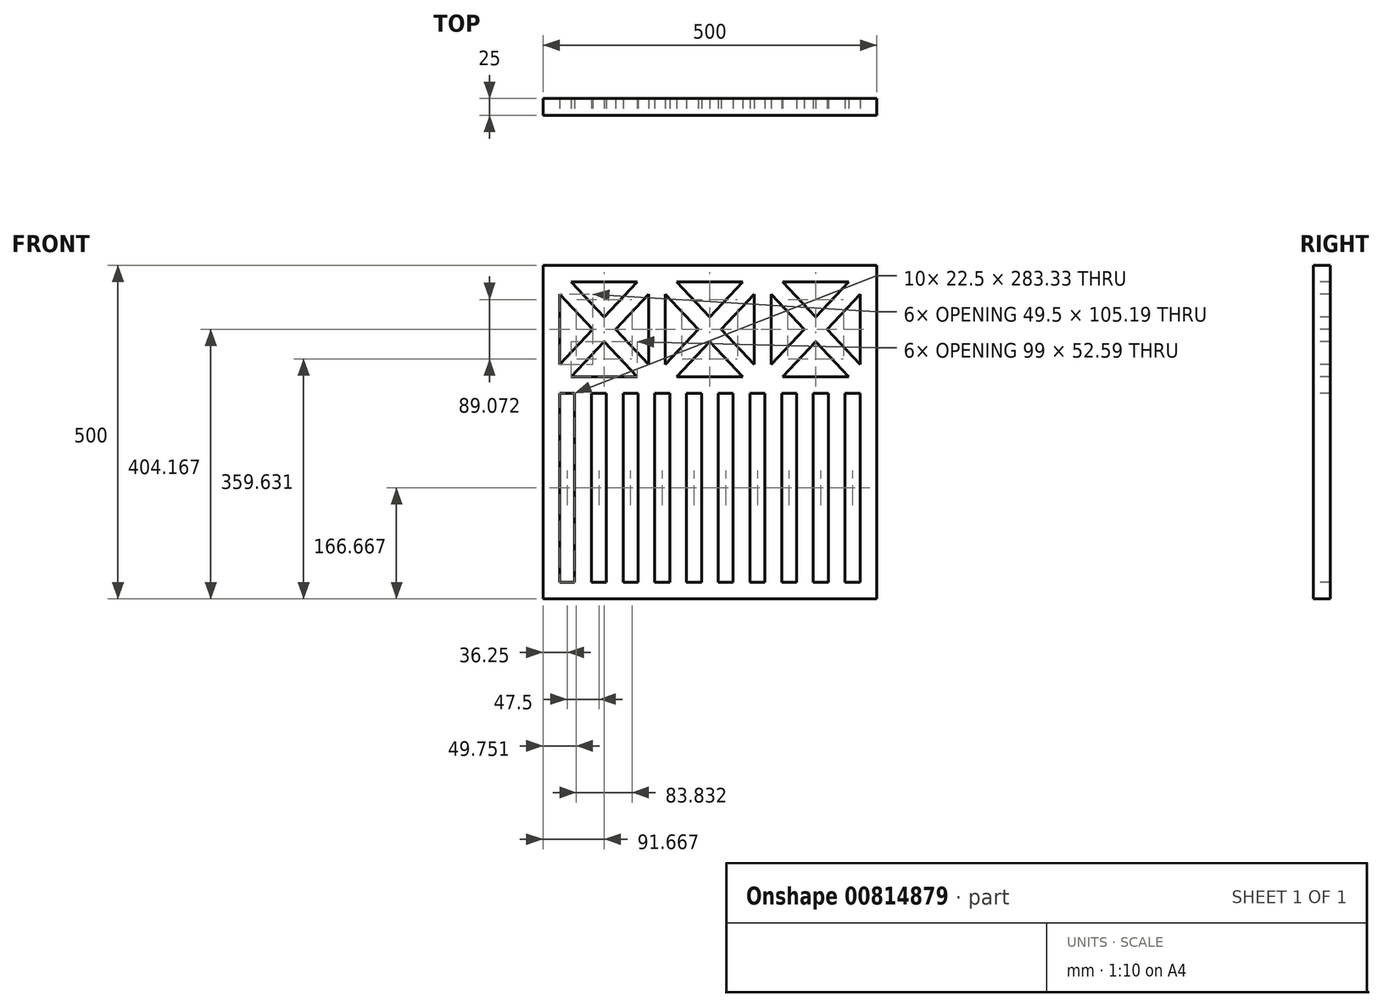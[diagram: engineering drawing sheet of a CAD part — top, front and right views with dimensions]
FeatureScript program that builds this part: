
annotation { "Feature Type Name" : "Feature", "Feature Type Description" : "" }
export const myFeature = defineFeature(function(context is Context, id is Id, definition is map)
    precondition{}
    {
        {
            var Q0;
            Q0=qCreatedBy(makeId("Front.planeOp"),FACE);
            var sketch = newSketch(context, id + "F0", { "sketchPlane" : qUnion([Q0])});
            skLineSegment(sketch, "E0.bottom", {"start": v(0, 0) * mm, "end": v(500, 0) * mm});
            skLineSegment(sketch, "E0.top", {"start": v(0, 500) * mm, "end": v(500, 500) * mm});
            skLineSegment(sketch, "E0.left", {"start": v(0, 0) * mm, "end": v(0, 500) * mm});
            skLineSegment(sketch, "E0.right", {"start": v(500, 0) * mm, "end": v(500, 500) * mm});
            skLineSegment(sketch, "E1.0", {"start": v(25, 25) * mm, "end": v(475, 25) * mm});
            skLineSegment(sketch, "E1.1", {"start": v(25, 25) * mm, "end": v(25, 475) * mm});
            skLineSegment(sketch, "E1.2", {"start": v(25, 475) * mm, "end": v(475, 475) * mm});
            skLineSegment(sketch, "E1.3", {"start": v(475, 25) * mm, "end": v(475, 475) * mm});
            skLineSegment(sketch, "E2", {"start": v(0, 500) * mm, "end": v(25, 475) * mm});
            skLineSegment(sketch, "E3", {"start": v(475, 475) * mm, "end": v(500, 500) * mm});
            skLineSegment(sketch, "E4", {"start": v(500, 0) * mm, "end": v(475, 25) * mm});
            skLineSegment(sketch, "E5", {"start": v(25, 25) * mm, "end": v(0, 0) * mm});
            skLineSegment(sketch, "E6", {"start": v(25, 333.33) * mm, "end": v(475, 333.33) * mm});
            skLineSegment(sketch, "E7", {"start": v(475, 308.33) * mm, "end": v(25, 308.33) * mm});
            skLineSegment(sketch, "E8", {"start": v(158.33, 475) * mm, "end": v(158.33, 333.33) * mm});
            skLineSegment(sketch, "E9", {"start": v(183.33, 475) * mm, "end": v(183.33, 333.33) * mm});
            skLineSegment(sketch, "E10", {"start": v(316.67, 475) * mm, "end": v(316.67, 333.33) * mm});
            skLineSegment(sketch, "E11", {"start": v(341.67, 475) * mm, "end": v(341.67, 333.33) * mm});
            skLineSegment(sketch, "E12", {"start": v(25, 475) * mm, "end": v(158.33, 333.33) * mm, "construction": true});
            skLineSegment(sketch, "E13.0", {"start": v(25, 456.76) * mm, "end": v(141.17, 333.33) * mm});
            skLineSegment(sketch, "E14.0", {"start": v(42.17, 475) * mm, "end": v(158.33, 351.57) * mm});
            skLineSegment(sketch, "E15", {"start": v(158.33, 475) * mm, "end": v(25, 333.33) * mm, "construction": true});
            skLineSegment(sketch, "E16.0", {"start": v(158.33, 456.76) * mm, "end": v(108.83, 404.17) * mm});
            skLineSegment(sketch, "E17.trimOffspring", {"start": v(91.67, 385.93) * mm, "end": v(42.17, 333.33) * mm});
            skLineSegment(sketch, "E18.0", {"start": v(141.17, 475) * mm, "end": v(91.67, 422.4) * mm});
            skLineSegment(sketch, "E19.trimOffspring", {"start": v(74.5, 404.17) * mm, "end": v(25, 351.57) * mm});
            skLineSegment(sketch, "E20.1.0.0", {"start": v(200.5, 475) * mm, "end": v(316.67, 351.57) * mm});
            skLineSegment(sketch, "E20.1.0.1", {"start": v(183.33, 456.76) * mm, "end": v(299.5, 333.33) * mm});
            skLineSegment(sketch, "E20.1.0.2", {"start": v(299.5, 475) * mm, "end": v(250, 422.4) * mm});
            skLineSegment(sketch, "E20.1.0.3", {"start": v(316.67, 456.76) * mm, "end": v(267.17, 404.17) * mm});
            skLineSegment(sketch, "E20.1.0.4", {"start": v(250, 385.93) * mm, "end": v(200.5, 333.33) * mm});
            skLineSegment(sketch, "E20.1.0.5", {"start": v(232.83, 404.17) * mm, "end": v(183.33, 351.57) * mm});
            skLineSegment(sketch, "E20.2.0.0", {"start": v(358.83, 475) * mm, "end": v(475, 351.57) * mm});
            skLineSegment(sketch, "E20.2.0.1", {"start": v(341.67, 456.76) * mm, "end": v(457.83, 333.33) * mm});
            skLineSegment(sketch, "E20.2.0.2", {"start": v(457.83, 475) * mm, "end": v(408.33, 422.4) * mm});
            skLineSegment(sketch, "E20.2.0.3", {"start": v(475, 456.76) * mm, "end": v(425.5, 404.17) * mm});
            skLineSegment(sketch, "E20.2.0.4", {"start": v(408.33, 385.93) * mm, "end": v(358.83, 333.33) * mm});
            skLineSegment(sketch, "E20.2.0.5", {"start": v(391.17, 404.17) * mm, "end": v(341.67, 351.57) * mm});
            skLineSegment(sketch, "E20.direction1", {"start": v(42.17, 475) * mm, "end": v(200.5, 475) * mm, "construction": true});
            skLineSegment(sketch, "E21", {"start": v(47.5, 308.33) * mm, "end": v(47.5, 25) * mm});
            skLineSegment(sketch, "E22", {"start": v(72.5, 308.33) * mm, "end": v(72.5, 25) * mm});
            skLineSegment(sketch, "E23.1.0.0", {"start": v(120, 308.33) * mm, "end": v(120, 25) * mm});
            skLineSegment(sketch, "E23.1.0.1", {"start": v(95, 308.33) * mm, "end": v(95, 25) * mm});
            skLineSegment(sketch, "E23.2.0.0", {"start": v(167.5, 308.33) * mm, "end": v(167.5, 25) * mm});
            skLineSegment(sketch, "E23.2.0.1", {"start": v(142.5, 308.33) * mm, "end": v(142.5, 25) * mm});
            skLineSegment(sketch, "E23.3.0.0", {"start": v(215, 308.33) * mm, "end": v(215, 25) * mm});
            skLineSegment(sketch, "E23.3.0.1", {"start": v(190, 308.33) * mm, "end": v(190, 25) * mm});
            skLineSegment(sketch, "E23.4.0.0", {"start": v(262.5, 308.33) * mm, "end": v(262.5, 25) * mm});
            skLineSegment(sketch, "E23.4.0.1", {"start": v(237.5, 308.33) * mm, "end": v(237.5, 25) * mm});
            skLineSegment(sketch, "E23.5.0.0", {"start": v(310, 308.33) * mm, "end": v(310, 25) * mm});
            skLineSegment(sketch, "E23.5.0.1", {"start": v(285, 308.33) * mm, "end": v(285, 25) * mm});
            skLineSegment(sketch, "E23.6.0.0", {"start": v(357.5, 308.33) * mm, "end": v(357.5, 25) * mm});
            skLineSegment(sketch, "E23.6.0.1", {"start": v(332.5, 308.33) * mm, "end": v(332.5, 25) * mm});
            skLineSegment(sketch, "E23.7.0.0", {"start": v(405, 308.33) * mm, "end": v(405, 25) * mm});
            skLineSegment(sketch, "E23.7.0.1", {"start": v(380, 308.33) * mm, "end": v(380, 25) * mm});
            skLineSegment(sketch, "E23.8.0.0", {"start": v(452.5, 308.33) * mm, "end": v(452.5, 25) * mm});
            skLineSegment(sketch, "E23.8.0.1", {"start": v(427.5, 308.33) * mm, "end": v(427.5, 25) * mm});
            skLineSegment(sketch, "E23.direction1", {"start": v(72.5, 25) * mm, "end": v(120, 25) * mm, "construction": true});
            skSolve(sketch);
        }
        {
            var Q0;
            Q0=makeQuery(id+"F0.imprint","IMPRINT",FACE,{"disambiguationData":[TD([[makeQuery(id+"F0.imprint","IMPRINT",EDGE,{"derivedFrom":sQuery(id+"F0.wireOp",EDGE,"E0.left")}),-1.0]])]});
            var Q1;
            Q1=makeQuery(id+"F0.imprint","IMPRINT",FACE,{"disambiguationData":[TD([[makeQuery(id+"F0.imprint","IMPRINT",EDGE,{"derivedFrom":sQuery(id+"F0.wireOp",EDGE,"E0.top")}),-1.0]])]});
            var Q2;
            Q2=makeQuery(id+"F0.imprint","IMPRINT",FACE,{"disambiguationData":[TD([[makeQuery(id+"F0.imprint","IMPRINT",EDGE,{"derivedFrom":sQuery(id+"F0.wireOp",EDGE,"E0.right")}),1.0]])]});
            var Q3;
            Q3=makeQuery(id+"F0.imprint","IMPRINT",FACE,{"disambiguationData":[TD([[makeQuery(id+"F0.imprint","IMPRINT",EDGE,{"derivedFrom":sQuery(id+"F0.wireOp",EDGE,"E0.bottom")}),1.0]])]});
            var Q4;
            {var subQ0=sQuery(id+"F0.wireOp",EDGE,"E17.trimOffspring");Q4=makeQuery(id+"F0.imprint","IMPRINT",FACE,{"disambiguationData":[TD([[makeQuery(id+"F0.imprint","IMPRINT",EDGE,{"derivedFrom":subQ0}),-1.0]])]});}
            var Q5;
            {var subQ0=sQuery(id+"F0.wireOp",EDGE,"E8");var subQ1=sQuery(id+"F0.wireOp",EDGE,"E6");var subQ2=makeQuery(id+"F0.imprint","INTERSECT",VERTEX,{"derivedFrom":[subQ1,subQ0]});Q5=makeQuery(id+"F0.imprint","IMPRINT",FACE,{"disambiguationData":[TD([[makeQuery(id+"F0.imprint","IMPRINT",EDGE,{"disambiguationData":[TD([[subQ2,1.0]])],"derivedFrom":subQ1}),1.0]])]});}
            var Q6;
            {var subQ0=sQuery(id+"F0.wireOp",EDGE,"E16.0");Q6=makeQuery(id+"F0.imprint","IMPRINT",FACE,{"disambiguationData":[TD([[makeQuery(id+"F0.imprint","IMPRINT",EDGE,{"derivedFrom":subQ0}),-1.0]])]});}
            var Q7;
            {var subQ0=sQuery(id+"F0.wireOp",EDGE,"E8");var subQ3=sQuery(id+"F0.wireOp",EDGE,"E1.2");var subQ4=makeQuery(id+"F0.imprint","INTERSECT",VERTEX,{"derivedFrom":[subQ3,subQ0]});Q7=makeQuery(id+"F0.imprint","IMPRINT",FACE,{"disambiguationData":[TD([[makeQuery(id+"F0.imprint","IMPRINT",EDGE,{"disambiguationData":[TD([[subQ4,-1.0]])],"derivedFrom":subQ3}),-1.0]])]});}
            var Q8;
            {var subQ5=sQuery(id+"F0.wireOp",EDGE,"E9");var subQ6=sQuery(id+"F0.wireOp",EDGE,"E1.2");var subQ7=makeQuery(id+"F0.imprint","INTERSECT",VERTEX,{"derivedFrom":[subQ6,subQ5]});Q8=makeQuery(id+"F0.imprint","IMPRINT",FACE,{"disambiguationData":[TD([[makeQuery(id+"F0.imprint","IMPRINT",EDGE,{"disambiguationData":[TD([[subQ7,-1.0]])],"derivedFrom":subQ6}),-1.0]])]});}
            var Q9;
            {var subQ0=sQuery(id+"F0.wireOp",EDGE,"E20.1.0.4");Q9=makeQuery(id+"F0.imprint","IMPRINT",FACE,{"disambiguationData":[TD([[makeQuery(id+"F0.imprint","IMPRINT",EDGE,{"derivedFrom":subQ0}),-1.0]])]});}
            var Q10;
            {var subQ0=sQuery(id+"F0.wireOp",EDGE,"E20.1.0.2");Q10=makeQuery(id+"F0.imprint","IMPRINT",FACE,{"disambiguationData":[TD([[makeQuery(id+"F0.imprint","IMPRINT",EDGE,{"derivedFrom":subQ0}),1.0]])]});}
            var Q11;
            {var subQ0=sQuery(id+"F0.wireOp",EDGE,"E10");var subQ1=sQuery(id+"F0.wireOp",EDGE,"E1.2");var subQ2=makeQuery(id+"F0.imprint","INTERSECT",VERTEX,{"derivedFrom":[subQ1,subQ0]});Q11=makeQuery(id+"F0.imprint","IMPRINT",FACE,{"disambiguationData":[TD([[makeQuery(id+"F0.imprint","IMPRINT",EDGE,{"disambiguationData":[TD([[subQ2,-1.0]])],"derivedFrom":subQ1}),-1.0]])]});}
            var Q12;
            {var subQ0=sQuery(id+"F0.wireOp",EDGE,"E11");var subQ1=sQuery(id+"F0.wireOp",EDGE,"E1.2");var subQ2=makeQuery(id+"F0.imprint","INTERSECT",VERTEX,{"derivedFrom":[subQ1,subQ0]});Q12=makeQuery(id+"F0.imprint","IMPRINT",FACE,{"disambiguationData":[TD([[makeQuery(id+"F0.imprint","IMPRINT",EDGE,{"disambiguationData":[TD([[subQ2,-1.0]])],"derivedFrom":subQ1}),-1.0]])]});}
            var Q13;
            {var subQ0=sQuery(id+"F0.wireOp",EDGE,"E20.2.0.2");Q13=makeQuery(id+"F0.imprint","IMPRINT",FACE,{"disambiguationData":[TD([[makeQuery(id+"F0.imprint","IMPRINT",EDGE,{"derivedFrom":subQ0}),1.0]])]});}
            var Q14;
            {var subQ0=sQuery(id+"F0.wireOp",EDGE,"E20.2.0.4");Q14=makeQuery(id+"F0.imprint","IMPRINT",FACE,{"disambiguationData":[TD([[makeQuery(id+"F0.imprint","IMPRINT",EDGE,{"derivedFrom":subQ0}),-1.0]])]});}
            var Q15;
            {var subQ12=sQuery(id+"F0.wireOp",EDGE,"E6");var subQ17=sQuery(id+"F0.wireOp",EDGE,"E1.1");var subQ18=makeQuery(id+"F0.imprint","INTERSECT",VERTEX,{"derivedFrom":[subQ17,subQ12]});Q15=makeQuery(id+"F0.imprint","IMPRINT",FACE,{"disambiguationData":[TD([[makeQuery(id+"F0.imprint","IMPRINT",EDGE,{"disambiguationData":[TD([[subQ18,1.0]])],"derivedFrom":subQ17}),-1.0]])]});}
            var Q16;
            {var subQ0=sQuery(id+"F0.wireOp",EDGE,"E21");Q16=makeQuery(id+"F0.imprint","IMPRINT",FACE,{"disambiguationData":[TD([[makeQuery(id+"F0.imprint","IMPRINT",EDGE,{"derivedFrom":subQ0}),1.0]])]});}
            var Q17;
            {var subQ0=sQuery(id+"F0.wireOp",EDGE,"E23.1.0.0");Q17=makeQuery(id+"F0.imprint","IMPRINT",FACE,{"disambiguationData":[TD([[makeQuery(id+"F0.imprint","IMPRINT",EDGE,{"derivedFrom":subQ0}),-1.0]])]});}
            var Q18;
            {var subQ0=sQuery(id+"F0.wireOp",EDGE,"E23.2.0.0");Q18=makeQuery(id+"F0.imprint","IMPRINT",FACE,{"disambiguationData":[TD([[makeQuery(id+"F0.imprint","IMPRINT",EDGE,{"derivedFrom":subQ0}),-1.0]])]});}
            var Q19;
            {var subQ0=sQuery(id+"F0.wireOp",EDGE,"E23.3.0.0");Q19=makeQuery(id+"F0.imprint","IMPRINT",FACE,{"disambiguationData":[TD([[makeQuery(id+"F0.imprint","IMPRINT",EDGE,{"derivedFrom":subQ0}),-1.0]])]});}
            var Q20;
            {var subQ0=sQuery(id+"F0.wireOp",EDGE,"E23.4.0.0");Q20=makeQuery(id+"F0.imprint","IMPRINT",FACE,{"disambiguationData":[TD([[makeQuery(id+"F0.imprint","IMPRINT",EDGE,{"derivedFrom":subQ0}),-1.0]])]});}
            var Q21;
            {var subQ0=sQuery(id+"F0.wireOp",EDGE,"E23.5.0.0");Q21=makeQuery(id+"F0.imprint","IMPRINT",FACE,{"disambiguationData":[TD([[makeQuery(id+"F0.imprint","IMPRINT",EDGE,{"derivedFrom":subQ0}),-1.0]])]});}
            var Q22;
            {var subQ0=sQuery(id+"F0.wireOp",EDGE,"E23.6.0.0");Q22=makeQuery(id+"F0.imprint","IMPRINT",FACE,{"disambiguationData":[TD([[makeQuery(id+"F0.imprint","IMPRINT",EDGE,{"derivedFrom":subQ0}),-1.0]])]});}
            var Q23;
            {var subQ0=sQuery(id+"F0.wireOp",EDGE,"E23.7.0.0");Q23=makeQuery(id+"F0.imprint","IMPRINT",FACE,{"disambiguationData":[TD([[makeQuery(id+"F0.imprint","IMPRINT",EDGE,{"derivedFrom":subQ0}),-1.0]])]});}
            var Q24;
            {var subQ0=sQuery(id+"F0.wireOp",EDGE,"E23.8.0.0");Q24=makeQuery(id+"F0.imprint","IMPRINT",FACE,{"disambiguationData":[TD([[makeQuery(id+"F0.imprint","IMPRINT",EDGE,{"derivedFrom":subQ0}),-1.0]])]});}
            extrude(context, id + "F1", {"entities" : qUnion([Q0, Q1, Q2, Q3, Q4, Q5, Q6, Q7, Q8, Q9, Q10, Q11, Q12, Q13, Q14, Q15, Q16, Q17, Q18, Q19, Q20, Q21, Q22, Q23, Q24]), "oppositeDirection" : true, "depth" : 25 * mm, "offsetDistance" : 25 * mm});
        }
    });
